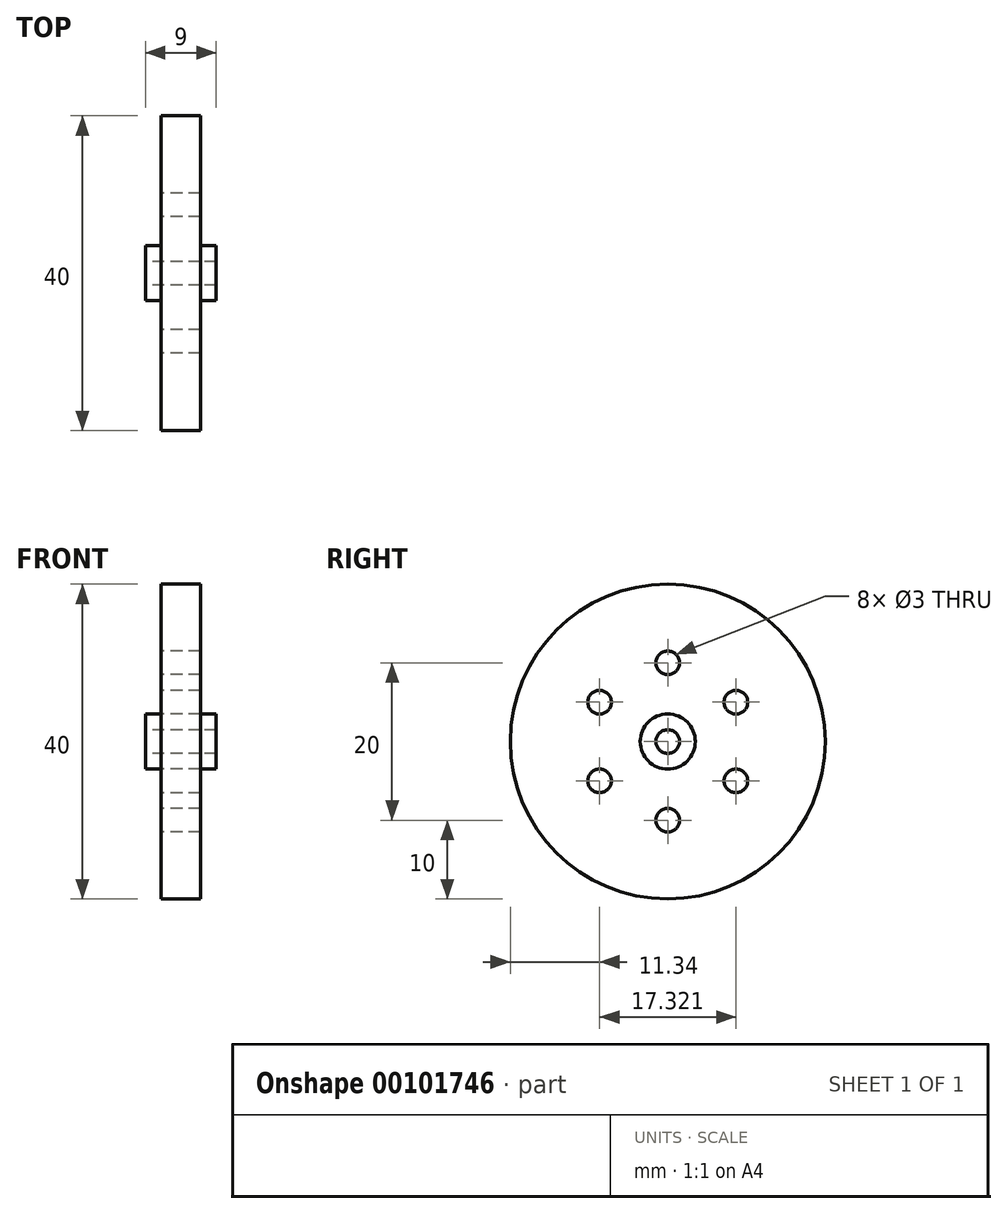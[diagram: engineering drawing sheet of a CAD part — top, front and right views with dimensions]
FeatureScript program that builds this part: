
annotation { "Feature Type Name" : "Feature", "Feature Type Description" : "" }
export const myFeature = defineFeature(function(context is Context, id is Id, definition is map)
    precondition{}
    {
        {
            var Q0;
            Q0=qCreatedBy(makeId("Right.planeOp"),FACE);
            var sketch = newSketch(context, id + "F0", { "sketchPlane" : qUnion([Q0])});
            skCircle(sketch, "E0", {"center": v(0, 0) * mm, "radius": 20 * mm});
            skLineSegment(sketch, "E1", {"start": v(0, 0) * mm, "end": v(0, 10) * mm});
            skCircle(sketch, "E2", {"center": v(0, 10) * mm, "radius": 1.5 * mm});
            skCircle(sketch, "E3.1.0", {"center": v(-8.66, 5) * mm, "radius": 1.5 * mm});
            skCircle(sketch, "E3.2.0", {"center": v(-8.66, -5) * mm, "radius": 1.5 * mm});
            skCircle(sketch, "E3.3.0", {"center": v(0, -10) * mm, "radius": 1.5 * mm});
            skCircle(sketch, "E3.4.0", {"center": v(8.66, -5) * mm, "radius": 1.5 * mm});
            skCircle(sketch, "E3.5.0", {"center": v(8.66, 5) * mm, "radius": 1.5 * mm});
            skCircle(sketch, "E4", {"center": v(0, 0) * mm, "radius": 1.5 * mm});
            skSolve(sketch);
        }
        {
            var Q0;
            Q0=qSketchRegion(id+"F0",true);
            extrude(context, id + "F1", {"entities" : qUnion([Q0]), "depth" : 5 * mm});
        }
        {
            var Q0;
            Q0=makeQuery(id+"F1.opExtrude","SWEPT_BODY",BODY,{"disambiguationData":[OSD([sQuery(id+"F0.wireOp",EDGE,"E0")])]});
            transform(context, id + "F2", {"entities" : qUnion([Q0]), "transformType" : TransformType.TRANSLATION_3D, "dx" : 0 * mm, "dy" : 0 * mm, "dz" : 0 * mm, "makeCopy" : true});
        }
        {
            var Q0;
            Q0=makeQuery(id+"F2.opPattern","COPY",BODY,{"derivedFrom":makeQuery(id+"F1.opExtrude","SWEPT_BODY",BODY,{"disambiguationData":[OSD([sQuery(id+"F0.wireOp",EDGE,"E0")])]}),"instanceName":"1"});
            transform(context, id + "F3", {"entities" : qUnion([Q0]), "transformType" : TransformType.TRANSLATION_3D, "dx" : 0 * mm, "dy" : 0 * mm, "dz" : 0 * mm, "makeCopy" : true});
        }
        {
            var Q0;
            Q0=makeQuery(id+"F3.opPattern","COPY",FACE,{"derivedFrom":makeQuery(id+"F2.opPattern","COPY",FACE,{"derivedFrom":makeQuery(id+"F1.opExtrude","CAP_FACE",FACE,{"disambiguationData":[OSD([sQuery(id+"F0.wireOp",EDGE,"E0"),sQuery(id+"F0.wireOp",EDGE,"E2"),sQuery(id+"F0.wireOp",EDGE,"E3.1.0"),sQuery(id+"F0.wireOp",EDGE,"E3.2.0"),sQuery(id+"F0.wireOp",EDGE,"E3.3.0"),sQuery(id+"F0.wireOp",EDGE,"E3.4.0"),sQuery(id+"F0.wireOp",EDGE,"E3.5.0")])],"isStart":false}),"instanceName":"1"}),"instanceName":"1"});
            var sketch = newSketch(context, id + "F4", { "sketchPlane" : qUnion([Q0])});
            skSolve(sketch);
        }
        {
            var Q0;
            Q0=makeQuery(id+"F4.imprint","IMPRINT",FACE,{"disambiguationData":[TD([[makeQuery(id+"F4.imprint","IMPRINT",EDGE,{"derivedFrom":makeQuery(id+"F3.opPattern","COPY",EDGE,{"derivedFrom":makeQuery(id+"F2.opPattern","COPY",EDGE,{"derivedFrom":makeQuery(id+"F1.opExtrude","CAP_EDGE",EDGE,{"disambiguationData":[OSD([sQuery(id+"F0.wireOp",EDGE,"E0")])],"isStart":false}),"instanceName":"1"}),"instanceName":"1"})}),1.0]])]});
            var sketch = newSketch(context, id + "F5", { "sketchPlane" : qUnion([Q0])});
            skCircle(sketch, "E5", {"center": v(0, 0) * mm, "radius": 3.5 * mm});
            skSolve(sketch);
        }
        {
            var Q0;
            Q0=makeQuery(id+"F5.imprint","IMPRINT",FACE,{"disambiguationData":[TD([[makeQuery(id+"F5.imprint","IMPRINT",EDGE,{"derivedFrom":sQuery(id+"F5.wireOp",EDGE,"E5")}),1.0]])]});
            var Q1;
            Q1=sQuery(id+"F0.wireOp",EDGE,"E4");
            var Q2;
            Q2=sQuery(id+"F5.wireOp",EDGE,"E5");
            extrude(context, id + "F6", {"entities" : qUnion([Q0]), "surfaceEntities" : qUnion([Q1, Q2]), "depth" : 2 * mm});
        }
        {
            var Q0;
            Q0=makeQuery(id+"F0.imprint","IMPRINT",FACE,{"disambiguationData":[TD([[makeQuery(id+"F0.imprint","IMPRINT",EDGE,{"derivedFrom":sQuery(id+"F0.wireOp",EDGE,"E0")}),1.0]])]});
            var sketch = newSketch(context, id + "F7", { "sketchPlane" : qUnion([Q0])});
            skCircle(sketch, "E6", {"center": v(0, 0) * mm, "radius": 3.5 * mm});
            skSolve(sketch);
        }
        {
            var Q0;
            Q0=makeQuery(id+"F7.imprint","IMPRINT",FACE,{"disambiguationData":[TD([[makeQuery(id+"F7.imprint","IMPRINT",EDGE,{"derivedFrom":sQuery(id+"F7.wireOp",EDGE,"E6")}),1.0]])]});
            var Q1;
            Q1=sQuery(id+"F7.wireOp",EDGE,"E6");
            extrude(context, id + "F8", {"entities" : qUnion([Q0]), "operationType" : NewBodyOperationType.ADD, "surfaceEntities" : qUnion([Q1]), "oppositeDirection" : true, "depth" : 2 * mm});
        }
    });
